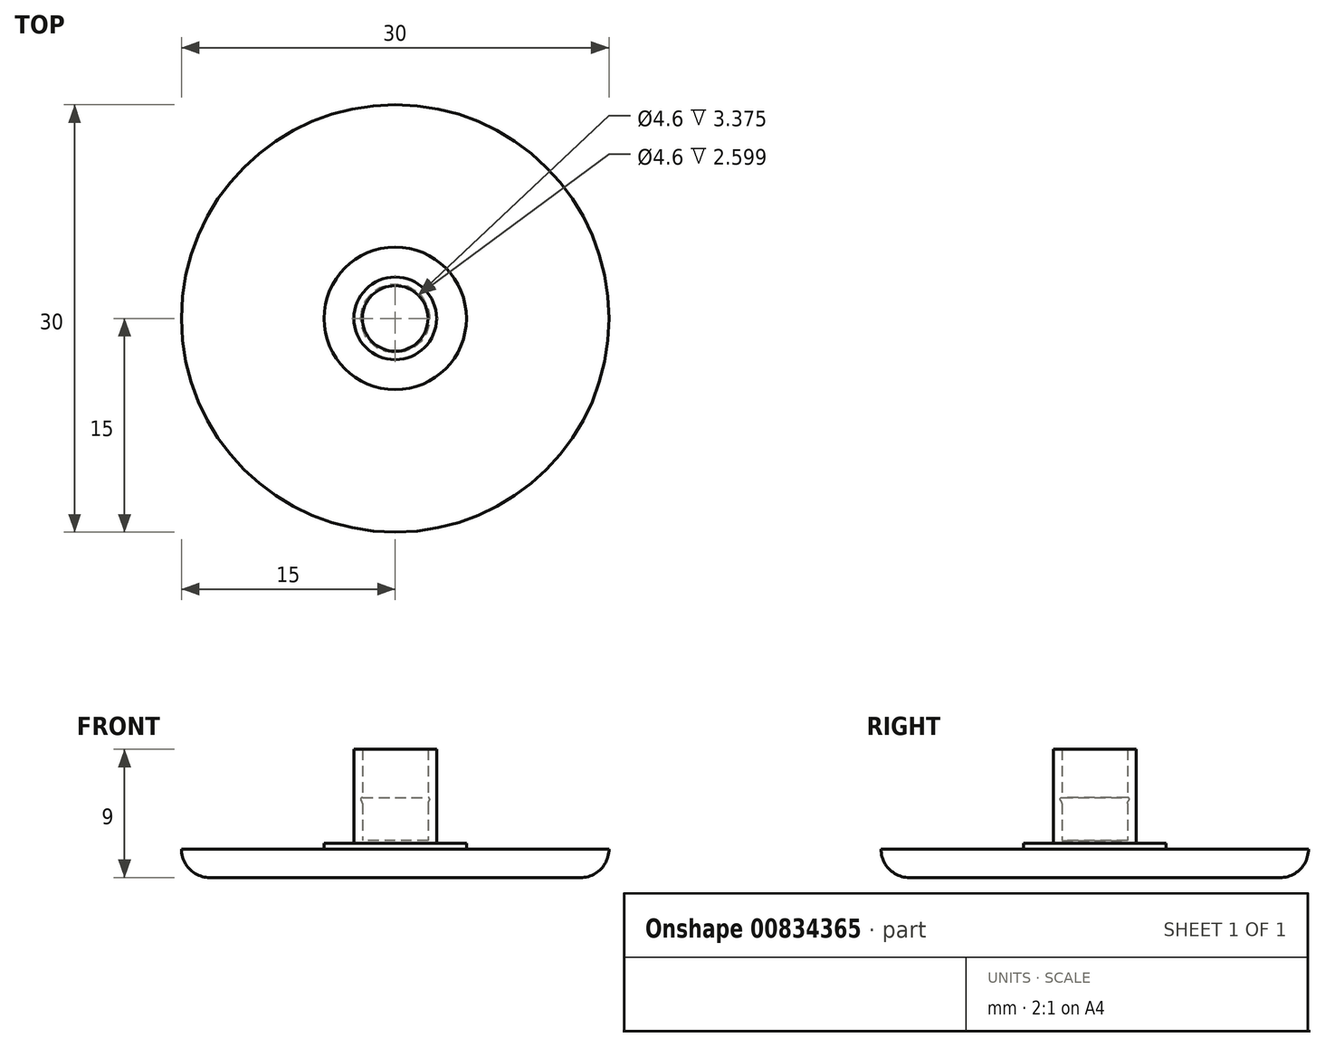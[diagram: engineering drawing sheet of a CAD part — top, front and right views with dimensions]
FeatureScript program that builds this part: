
annotation { "Feature Type Name" : "Feature", "Feature Type Description" : "" }
export const myFeature = defineFeature(function(context is Context, id is Id, definition is map)
    precondition{}
    {
        {
            var Q0;
            Q0=qCreatedBy(makeId("Top.planeOp"),FACE);
            var sketch = newSketch(context, id + "F0", { "sketchPlane" : qUnion([Q0])});
            skCircle(sketch, "E0", {"center": v(0, 0) * mm, "radius": 2.9 * mm});
            skCircle(sketch, "E1", {"center": v(0, 0) * mm, "radius": 15 * mm});
            skCircle(sketch, "E2", {"center": v(0, 0) * mm, "radius": 5 * mm});
            skSolve(sketch);
        }
        {
            var Q0;
            Q0=makeQuery(id+"F0.imprint","IMPRINT",FACE,{"disambiguationData":[TD([[makeQuery(id+"F0.imprint","IMPRINT",EDGE,{"derivedFrom":sQuery(id+"F0.wireOp",EDGE,"E0")}),1.0]])]});
            extrude(context, id + "F1", {"entities" : qUnion([Q0]), "depth" : 7 * mm, "offsetDistance" : 25 * mm});
        }
        {
            var Q0;
            Q0=makeQuery(id+"F1.opExtrude","CAP_FACE",FACE,{"disambiguationData":[OSD([sQuery(id+"F0.wireOp",EDGE,"E0")])],"isStart":false});
            shell(context, id + "F2", {"entities" : qUnion([Q0]), "thickness" : 0.6 * mm});
        }
        {
            var Q0;
            Q0=makeQuery(id+"F0.imprint","IMPRINT",FACE,{"disambiguationData":[TD([[makeQuery(id+"F0.imprint","IMPRINT",EDGE,{"derivedFrom":sQuery(id+"F0.wireOp",EDGE,"E0")}),1.0]])]});
            var Q1;
            Q1=makeQuery(id+"F0.imprint","IMPRINT",FACE,{"disambiguationData":[TD([[makeQuery(id+"F0.imprint","IMPRINT",EDGE,{"derivedFrom":sQuery(id+"F0.wireOp",EDGE,"E1")}),1.0]])]});
            var Q2;
            Q2=makeQuery(id+"F0.imprint","IMPRINT",FACE,{"disambiguationData":[TD([[makeQuery(id+"F0.imprint","IMPRINT",EDGE,{"derivedFrom":sQuery(id+"F0.wireOp",EDGE,"E0")}),-1.0]])]});
            extrude(context, id + "F3", {"entities" : qUnion([Q0, Q1, Q2]), "operationType" : NewBodyOperationType.ADD, "oppositeDirection" : true, "depth" : 2 * mm, "offsetDistance" : 25 * mm});
        }
        {
            var Q0;
            Q0=makeQuery(id+"F3.opExtrude","CAP_EDGE",EDGE,{"disambiguationData":[OSD([sQuery(id+"F0.wireOp",EDGE,"E1")])],"isStart":false});
            fillet(context, id + "F4", {"entities" : qUnion([Q0]), "radius" : 2 * mm, "tangentPropagation" : true, "allowEdgeOverflow" : false});
        }
        {
            var Q0;
            Q0=qCreatedBy(makeId("Front.planeOp"),FACE);
            var sketch = newSketch(context, id + "F5", { "sketchPlane" : qUnion([Q0])});
            skLineSegment(sketch, "E3.bottom", {"start": v(0, 0) * mm, "end": v(2.3, 0) * mm});
            skLineSegment(sketch, "E3.top", {"start": v(0, 3.5) * mm, "end": v(2.3, 3.5) * mm});
            skLineSegment(sketch, "E3.left", {"start": v(0, 0) * mm, "end": v(0, 3.5) * mm});
            skLineSegment(sketch, "E3.right", {"start": v(2.3, 0) * mm, "end": v(2.3, 3.5) * mm});
            skCircle(sketch, "E4", {"center": v(2.3, 3.5) * mm, "radius": 0.12 * mm});
            skSolve(sketch);
        }
        {
            var Q0;
            {var subQ0=sQuery(id+"F5.wireOp",EDGE,"E3.right");var subQ1=sQuery(id+"F5.wireOp",EDGE,"E3.top");var subQ2=makeQuery(id+"F5.imprint","INTERSECT",VERTEX,{"derivedFrom":[subQ1,subQ0]});Q0=makeQuery(id+"F5.imprint","IMPRINT",FACE,{"disambiguationData":[TD([[makeQuery(id+"F5.imprint","IMPRINT",EDGE,{"disambiguationData":[TD([[subQ2,1.0]])],"derivedFrom":subQ1}),-1.0]])]});}
            var Q1;
            {var subQ0=sQuery(id+"F5.wireOp",EDGE,"E3.right");var subQ1=sQuery(id+"F5.wireOp",EDGE,"E3.top");var subQ2=makeQuery(id+"F5.imprint","INTERSECT",VERTEX,{"derivedFrom":[subQ1,subQ0]});Q1=makeQuery(id+"F5.imprint","IMPRINT",FACE,{"disambiguationData":[TD([[makeQuery(id+"F5.imprint","IMPRINT",EDGE,{"disambiguationData":[TD([[subQ2,1.0]])],"derivedFrom":subQ1}),1.0]])]});}
            var Q2;
            Q2=sQuery(id+"F5.wireOp",EDGE,"E3.left");
            revolve(context, id + "F6", {"operationType" : NewBodyOperationType.REMOVE, "surfaceOperationType" : NewSurfaceOperationType.NEW, "entities" : qUnion([Q0, Q1]), "axis" : qUnion([Q2]), "revolveType" : RevolveType.TWO_DIRECTIONS, "angle" : 180 * degree, "angleBack" : 180 * degree});
        }
        {
            var Q0;
            {var subQ0=sQuery(id+"F0.wireOp",EDGE,"E0");Q0=makeQuery(id+"F6.boolean.opBoolean","INTERSECT",EDGE,{"disambiguationData":[OD(0.0)],"derivedFrom":[makeQuery(id+"F2.opShell","OFFSET_FACE",FACE,{"disambiguationData":[OSD([subQ0]),TDD([makeQuery(id+"F1.opExtrude","SWEPT_FACE",FACE,{"disambiguationData":[OSD([subQ0])]})])]}),makeQuery(id+"F6.opRevolve","SWEPT_FACE",FACE,{"disambiguationData":[OSD([sQuery(id+"F5.wireOp",EDGE,"E4")])]})]});}
            fillet(context, id + "F7", {"entities" : qUnion([Q0]), "radius" : 0.3 * mm, "tangentPropagation" : true, "allowEdgeOverflow" : false});
        }
        {
            var Q0;
            Q0=makeQuery(id+"F0.imprint","IMPRINT",FACE,{"disambiguationData":[TD([[makeQuery(id+"F0.imprint","IMPRINT",EDGE,{"derivedFrom":sQuery(id+"F0.wireOp",EDGE,"E0")}),-1.0]])]});
            extrude(context, id + "F8", {"entities" : qUnion([Q0]), "operationType" : NewBodyOperationType.ADD, "depth" : 0.4 * mm, "offsetDistance" : 25 * mm});
        }
    });
